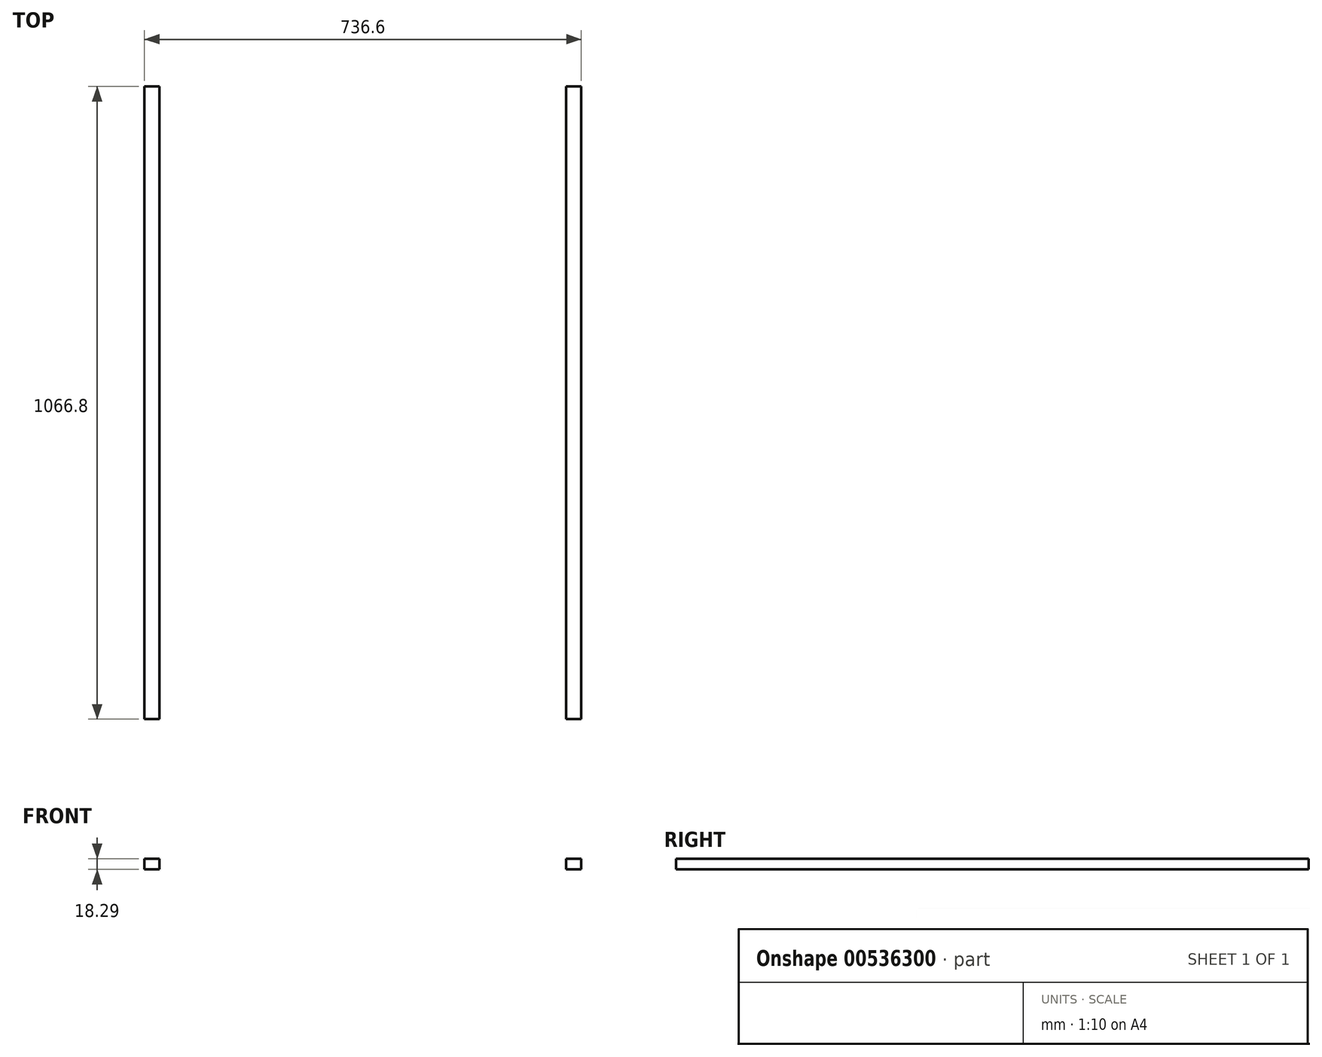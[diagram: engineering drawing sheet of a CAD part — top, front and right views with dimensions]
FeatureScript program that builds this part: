
annotation { "Feature Type Name" : "Feature", "Feature Type Description" : "" }
export const myFeature = defineFeature(function(context is Context, id is Id, definition is map)
    precondition{}
    {
        {
            var Q0;
            Q0=qCreatedBy(makeId("Top.planeOp"),FACE);
            var sketch = newSketch(context, id + "F0", { "sketchPlane" : qUnion([Q0])});
            skLineSegment(sketch, "E0.bottom", {"start": v(1229.57, 1143.1) * mm, "end": v(2448.77, 1143.1) * mm});
            skLineSegment(sketch, "E0.top", {"start": v(1229.57, -482.5) * mm, "end": v(2448.77, -482.5) * mm});
            skLineSegment(sketch, "E0.left", {"start": v(1229.57, 1143.1) * mm, "end": v(1229.57, -482.5) * mm});
            skLineSegment(sketch, "E0.right", {"start": v(2448.77, 1143.1) * mm, "end": v(2448.77, -482.5) * mm});
            skLineSegment(sketch, "E1", {"start": v(1229.57, -482.5) * mm, "end": v(1331.17, -482.5) * mm});
            skLineSegment(sketch, "E2", {"start": v(1331.17, -482.5) * mm, "end": v(1331.17, -25.3) * mm});
            skLineSegment(sketch, "E3", {"start": v(1331.17, -25.3) * mm, "end": v(1407.37, -25.3) * mm});
            skLineSegment(sketch, "E4", {"start": v(1407.37, -25.3) * mm, "end": v(1407.37, -482.5) * mm});
            skLineSegment(sketch, "E5", {"start": v(2448.77, -482.5) * mm, "end": v(2347.17, -482.5) * mm});
            skLineSegment(sketch, "E6", {"start": v(2347.17, -482.5) * mm, "end": v(2347.17, -25.3) * mm});
            skLineSegment(sketch, "E7", {"start": v(2347.17, -25.3) * mm, "end": v(2270.97, -25.3) * mm});
            skLineSegment(sketch, "E8", {"start": v(2270.97, -25.3) * mm, "end": v(2270.97, -482.5) * mm});
            skLineSegment(sketch, "E9", {"start": v(1229.57, -482.5) * mm, "end": v(1229.57, 76.3) * mm});
            skLineSegment(sketch, "E10", {"start": v(1229.57, 76.3) * mm, "end": v(1470.87, 76.3) * mm});
            skLineSegment(sketch, "E11", {"start": v(1470.87, 76.3) * mm, "end": v(1470.87, 1143.1) * mm});
            skLineSegment(sketch, "E12", {"start": v(2448.77, 76.3) * mm, "end": v(2207.47, 76.3) * mm});
            skLineSegment(sketch, "E13", {"start": v(2207.47, 76.3) * mm, "end": v(2207.47, 1143.1) * mm});
            skLineSegment(sketch, "E14", {"start": v(1470.87, 76.3) * mm, "end": v(1496.27, 76.3) * mm});
            skLineSegment(sketch, "E15", {"start": v(1496.27, 76.3) * mm, "end": v(1496.27, 285.86) * mm});
            skLineSegment(sketch, "E16.bottom", {"start": v(1496.27, 285.86) * mm, "end": v(1514.56, 285.86) * mm});
            skLineSegment(sketch, "E16.top", {"start": v(1496.27, 362.06) * mm, "end": v(1514.56, 362.06) * mm});
            skLineSegment(sketch, "E16.left", {"start": v(1496.27, 285.86) * mm, "end": v(1496.27, 362.06) * mm});
            skLineSegment(sketch, "E16.right", {"start": v(1514.56, 285.86) * mm, "end": v(1514.56, 362.06) * mm});
            skLineSegment(sketch, "E17", {"start": v(1496.27, 362.06) * mm, "end": v(1496.27, 571.6) * mm});
            skLineSegment(sketch, "E18.bottom", {"start": v(1496.27, 571.6) * mm, "end": v(1514.56, 571.6) * mm});
            skLineSegment(sketch, "E18.top", {"start": v(1496.27, 647.8) * mm, "end": v(1514.56, 647.8) * mm});
            skLineSegment(sketch, "E18.left", {"start": v(1496.27, 571.6) * mm, "end": v(1496.27, 647.8) * mm});
            skLineSegment(sketch, "E18.right", {"start": v(1514.56, 571.6) * mm, "end": v(1514.56, 647.8) * mm});
            skLineSegment(sketch, "E19", {"start": v(1496.27, 647.8) * mm, "end": v(1496.27, 857.36) * mm});
            skLineSegment(sketch, "E20.bottom", {"start": v(1496.27, 857.36) * mm, "end": v(1514.56, 857.36) * mm});
            skLineSegment(sketch, "E20.top", {"start": v(1496.27, 933.56) * mm, "end": v(1514.56, 933.56) * mm});
            skLineSegment(sketch, "E20.left", {"start": v(1496.27, 857.36) * mm, "end": v(1496.27, 933.56) * mm});
            skLineSegment(sketch, "E20.right", {"start": v(1514.56, 857.36) * mm, "end": v(1514.56, 933.56) * mm});
            skLineSegment(sketch, "E21", {"start": v(2207.47, 76.3) * mm, "end": v(2182.07, 76.3) * mm});
            skLineSegment(sketch, "E22", {"start": v(2182.07, 76.3) * mm, "end": v(2182.07, 285.86) * mm});
            skLineSegment(sketch, "E23.bottom", {"start": v(2182.07, 285.86) * mm, "end": v(2163.78, 285.86) * mm});
            skLineSegment(sketch, "E23.top", {"start": v(2182.07, 362.06) * mm, "end": v(2163.78, 362.06) * mm});
            skLineSegment(sketch, "E23.left", {"start": v(2182.07, 285.86) * mm, "end": v(2182.07, 362.06) * mm});
            skLineSegment(sketch, "E23.right", {"start": v(2163.78, 285.86) * mm, "end": v(2163.78, 362.06) * mm});
            skLineSegment(sketch, "E24", {"start": v(2182.07, 362.06) * mm, "end": v(2182.07, 571.6) * mm});
            skLineSegment(sketch, "E25.bottom", {"start": v(2182.07, 571.6) * mm, "end": v(2163.78, 571.6) * mm});
            skLineSegment(sketch, "E25.top", {"start": v(2182.07, 647.8) * mm, "end": v(2163.78, 647.8) * mm});
            skLineSegment(sketch, "E25.left", {"start": v(2182.07, 571.6) * mm, "end": v(2182.07, 647.8) * mm});
            skLineSegment(sketch, "E25.right", {"start": v(2163.78, 571.6) * mm, "end": v(2163.78, 647.8) * mm});
            skLineSegment(sketch, "E26", {"start": v(2182.07, 647.8) * mm, "end": v(2182.07, 857.36) * mm});
            skLineSegment(sketch, "E27.bottom", {"start": v(2182.07, 857.36) * mm, "end": v(2163.78, 857.36) * mm});
            skLineSegment(sketch, "E27.top", {"start": v(2182.07, 933.56) * mm, "end": v(2163.78, 933.56) * mm});
            skLineSegment(sketch, "E27.left", {"start": v(2182.07, 857.36) * mm, "end": v(2182.07, 933.56) * mm});
            skLineSegment(sketch, "E27.right", {"start": v(2163.78, 857.36) * mm, "end": v(2163.78, 933.56) * mm});
            skLineSegment(sketch, "E28", {"start": v(2182.07, 933.56) * mm, "end": v(2182.07, 1143.1) * mm});
            skLineSegment(sketch, "E29", {"start": v(1496.27, 933.56) * mm, "end": v(1496.27, 1143.1) * mm});
            skSolve(sketch);
        }
        {
            var Q0;
            Q0=makeQuery(id+"F0.imprint","IMPRINT",FACE,{"disambiguationData":[TD([[makeQuery(id+"F0.imprint","IMPRINT",EDGE,{"derivedFrom":sQuery(id+"F0.wireOp",EDGE,"E1")}),1.0]])]});
            var Q1;
            {var subQ1=sQuery(id+"F0.wireOp",EDGE,"E11");Q1=makeQuery(id+"F0.imprint","IMPRINT",FACE,{"disambiguationData":[TD([[makeQuery(id+"F0.imprint","IMPRINT",EDGE,{"derivedFrom":subQ1}),-1.0]])]});}
            var Q2;
            {var subQ0=sQuery(id+"F0.wireOp",EDGE,"E13");Q2=makeQuery(id+"F0.imprint","IMPRINT",FACE,{"disambiguationData":[TD([[makeQuery(id+"F0.imprint","IMPRINT",EDGE,{"derivedFrom":subQ0}),1.0]])]});}
            extrude(context, id + "F1", {"entities" : qUnion([Q0, Q1, Q2]), "depth" : 18.29 * mm, "offsetDistance" : 25.4 * mm});
        }
    });
